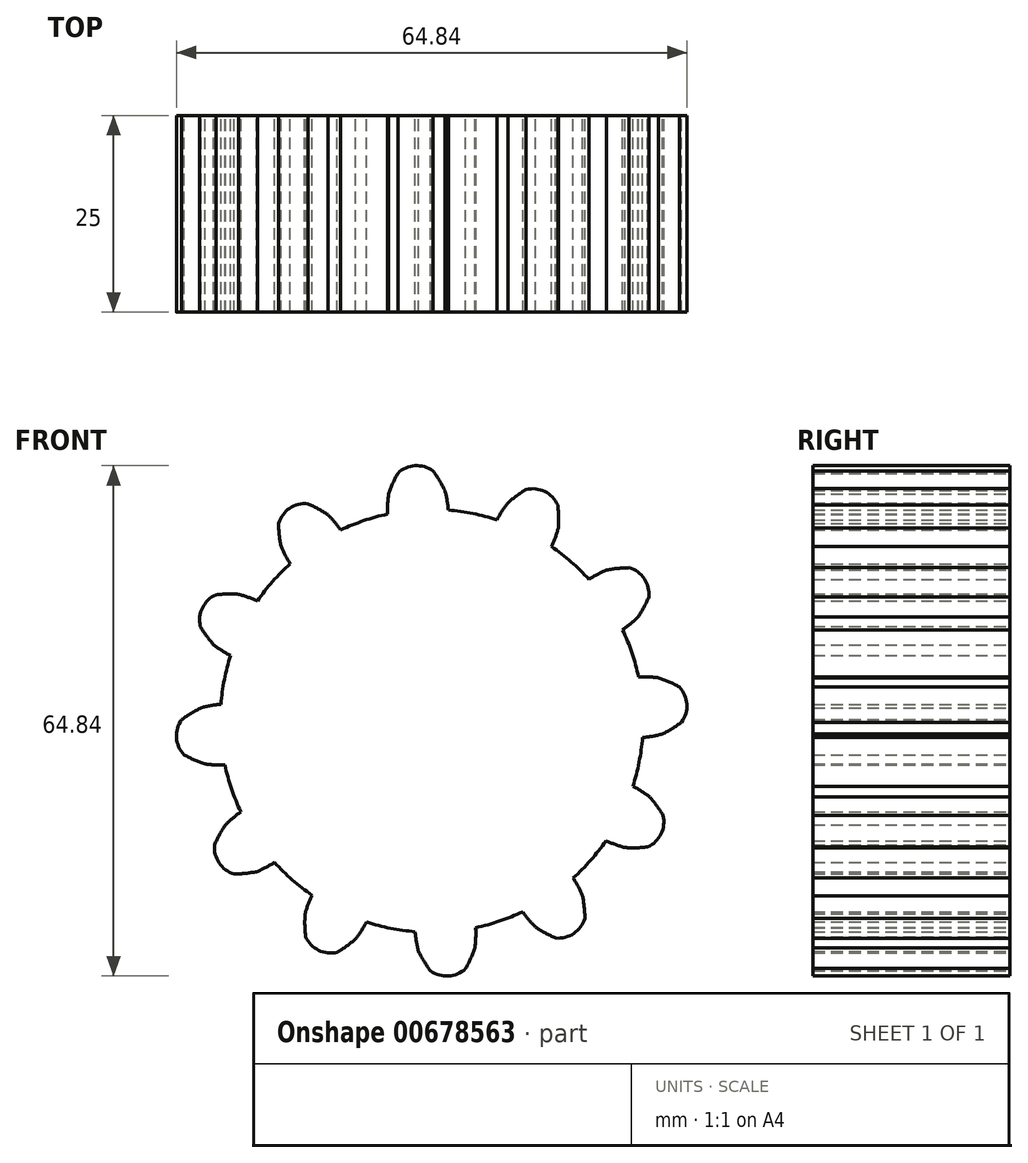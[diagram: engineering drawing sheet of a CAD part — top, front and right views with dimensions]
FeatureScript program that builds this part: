
annotation { "Feature Type Name" : "Feature", "Feature Type Description" : "" }
export const myFeature = defineFeature(function(context is Context, id is Id, definition is map)
    precondition{}
    {
        {
            var Q0;
            Q0=qCreatedBy(makeId("Front.planeOp"),FACE);
            var sketch = newSketch(context, id + "F0", { "sketchPlane" : qUnion([Q0])});
            skCircle(sketch, "E0", {"center": v(0, 0) * mm, "radius": 26.86 * mm});
            skCircle(sketch, "E1", {"center": v(0, 0) * mm, "radius": 29.34 * mm, "construction": true});
            skCircle(sketch, "E2", {"center": v(0, 0) * mm, "radius": 31.75 * mm, "construction": true});
            skLineSegment(sketch, "E3", {"start": v(1.67, 29.29) * mm, "end": v(-81.07, 29.29) * mm, "construction": true});
            skLineSegment(sketch, "E4", {"start": v(1.67, 29.29) * mm, "end": v(-74.84, 1.44) * mm, "construction": true});
            skCircle(sketch, "E5", {"center": v(0, 0) * mm, "radius": 26.95 * mm, "construction": true});
            skLineSegment(sketch, "E6", {"start": v(0, 0) * mm, "end": v(-5.28, 80.55) * mm, "construction": true});
            skLineSegment(sketch, "E7", {"start": v(0, 0) * mm, "end": v(0, 81.78) * mm, "construction": true});
            skCircle(sketch, "E8", {"center": v(1.67, 29.29) * mm, "radius": 7.3 * mm, "construction": true});
            skCircle(sketch, "E9", {"center": v(-5.2, 26.8) * mm, "radius": 7.3 * mm, "construction": true});
            skArc(sketch, "E10", {"start": v(2.1, 26.78) * mm, "mid": v(1.95, 28.04) * mm, "end": v(1.67, 29.29) * mm});
            skArc(sketch, "E11", {"start": v(1.67, 29.29) * mm, "mid": v(0.97, 30.55) * mm, "end": v(0.17, 31.75) * mm});
            skArc(sketch, "E12.MirrorCS", {"start": v(-5.48, 28.82) * mm, "mid": v(-4.95, 30.17) * mm, "end": v(-4.3, 31.46) * mm});
            skArc(sketch, "E13.MirrorCS", {"start": v(-5.58, 26.27) * mm, "mid": v(-5.59, 27.55) * mm, "end": v(-5.48, 28.82) * mm});
            skLineSegment(sketch, "E14", {"start": v(0, 0) * mm, "end": v(0, -28.53) * mm, "construction": true});
            skCircle(sketch, "E15", {"center": v(0, 0) * mm, "radius": 12.01 * mm});
            skLineSegment(sketch, "E16", {"start": v(-4.02, 11.32) * mm, "end": v(-4.02, -11.32) * mm});
            skLineSegment(sketch, "E17.MirrorCS", {"start": v(4.02, 11.32) * mm, "end": v(4.02, -11.32) * mm});
            skArc(sketch, "E18", {"start": v(0.17, 31.75) * mm, "mid": v(-2.12, 32.41) * mm, "end": v(-4.3, 31.46) * mm});
            skSolve(sketch);
        }
        {
            var Q0;
            {var subQ0=sQuery(id+"F0.wireOp",EDGE,"E16");Q0=makeQuery(id+"F0.imprint","IMPRINT",FACE,{"disambiguationData":[TD([[makeQuery(id+"F0.imprint","IMPRINT",EDGE,{"derivedFrom":subQ0}),1.0]])]});}
            var Q1;
            {var subQ6=sQuery(id+"F0.wireOp",EDGE,"E0");var subQ7=makeQuery(id+"F0.imprint","INTERSECT",VERTEX,{"derivedFrom":[subQ6,sQuery(id+"F0.wireOp",EDGE,"E10")]});Q1=makeQuery(id+"F0.imprint","IMPRINT",FACE,{"disambiguationData":[TD([[makeQuery(id+"F0.imprint","IMPRINT",EDGE,{"disambiguationData":[TD([[subQ7,-1.0]])],"derivedFrom":subQ6}),1.0]])]});}
            extrude(context, id + "F1", {"entities" : qUnion([Q0, Q1]), "depth" : 25 * mm, "offsetDistance" : 25 * mm});
        }
        {
            var Q0;
            {var subQ0=sQuery(id+"F0.wireOp",EDGE,"E10");Q0=makeQuery(id+"F0.imprint","IMPRINT",FACE,{"disambiguationData":[TD([[makeQuery(id+"F0.imprint","IMPRINT",EDGE,{"derivedFrom":subQ0}),1.0]])]});}
            extrude(context, id + "F2", {"entities" : qUnion([Q0]), "operationType" : NewBodyOperationType.ADD, "depth" : 25 * mm, "offsetDistance" : 25 * mm});
        }
        {
            var Q0;
            Q0=makeQuery(id+"F1.opExtrude","SWEPT_BODY",BODY,{"disambiguationData":[OSD([sQuery(id+"F0.wireOp",EDGE,"E0"),sQuery(id+"F0.wireOp",EDGE,"E15"),sQuery(id+"F0.wireOp",EDGE,"E16"),sQuery(id+"F0.wireOp",EDGE,"E17.MirrorCS")])]});
            var Q1;
            Q1=makeQuery(id+"F1.opExtrude","SWEPT_FACE",FACE,{"disambiguationData":[OSD([sQuery(id+"F0.wireOp",EDGE,"E0")])]});
            circularPattern(context, id + "F3", {"operationType" : NewBodyOperationType.ADD, "entities" : qUnion([Q0]), "axis" : qUnion([Q1]), "angle" : 360 * degree, "instanceCount" : 12, "equalSpace" : true});
        }
    });
